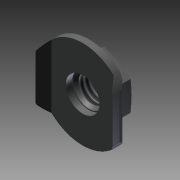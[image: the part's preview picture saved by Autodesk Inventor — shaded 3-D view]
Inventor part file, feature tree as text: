
AUTODESK INVENTOR PART (.ipt)
format: ipt  version: 2011 SP1 (Build 150282100, 282)  size: 163,840 bytes
history: native  units: mm
features: other x14, sketch x5, extrude x3, revolve x2, thread x1
ambient origin geometry x8: Origin, YZ Plane, XZ Plane, XY Plane, X Axis, Y Axis, Z Axis, Center Point
bodies: Solid1 (feature_tree)
feature tree (25):
  extrude  "Extrusion1"  TaperAngle=360.0deg  [1 undecoded]
  revolve  "Revolution1"  [1 undecoded]
  extrude  "Extrusion2"  Depth=1.834mm TaperAngle=0.0deg
  extrude  "Extrusion3"  [1 undecoded]
  revolve  "Revolution2"  [1 undecoded]
  thread  "Thread1"  [1 undecoded]
  other  "FS1_XY"
  other  "FS1_YZ"
  other  "FS1_ZX"
  other  "FS1_X"
  other  "FS1_Y"
  other  "FS1_Z"
  other  "FS1_Center"
  other  "FS2_XY"
  other  "FS2_YZ"
  other  "FS2_ZX"
  other  "FS2_X"
  other  "FS2_Y"
  other  "FS2_Z"
  other  "FS2_Center"
  sketch  "Skizze_1"  dims[d0=14.0mm d1=0.0mm d2=360.0deg]
  sketch  "Skizze_2"  dims[d7=360.0deg d8=1.834mm d9=0.0mm]
  sketch  "Skizze_3"
  sketch  "Skizze_4"
  sketch  "Skizze_5_ALT_Drilling_1"  dims[d3=2.7mm d4=0.0mm d5=10.0mm d6=0.0mm]
note: 5 required parameter values undecoded (feature->parameter linkage not recoverable at this tier; creation-order binding heuristic only, values carry confidence <= 0.55)